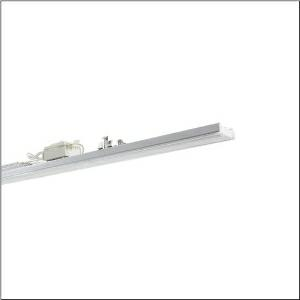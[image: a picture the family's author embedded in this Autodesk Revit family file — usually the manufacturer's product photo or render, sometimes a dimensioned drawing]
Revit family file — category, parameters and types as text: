
# Revit family: licross_11_recessed_mo_51te127n485g
name_source: partatom
category: Lighting Fixtures
units: mm (PartAtom-declared; Revit-internal decimal feet)

## family parameters
Cut with Voids When Loaded = No
Host = Face
Light Source = No
Part Type = Normal
Room Calculation Point = No
Round Connector Dimension = Use Diameter
Shared = No

## types (1)
- Licross 11 Recessed MO (1 x LED, 8950 lm, 48.5 W, 4000K)
    Apparent Load = 49 VA
    CIE Flux Codes = 67 92 99 100 100
    Color Rendering = 80
    Color Temperature = 4000K
    Default Elevation = 1800 mm
    Description = Licross 11 Recessed MO, luminaire insert, of sheet steel, galvanised, coil coated, white, length: 1.500mm, width: 66mm, height: 67mm, LED rated luminous flux: 8.950lm, light colour: 840, SDCM (Standard Deviation of Colour Matching)MacAdam ≤ 2 SDCM (initial), control gear: ON/OFF, with plug, 3-pole, with phase selection, mains connection: 220..240V, AC, 50/60Hz, rated input power: 49W, internal wiring halogen-free, primary optical cover: cover, of PMMA, light emission: direct distribution, primary light characteristic: symmetric, protection rating (complete): IP54, insulation class (complete): insulation class I (protective earthing), certification: CE, ENEC, VDE, UKCA, protection symbol: D if used in an environment with non-conductive dust loads with corresponding accessories, impact resistance: IK06, permissible ambient temperature for indoor applications: -35..+35°C, corresponds to IFS (International Featured Standards) requirements for safety and quality in the food industry, reducing of maximum allowable ambient temperature of 5°C with ceiling mounting, The light source and the operating device comply with the requirements of the Ecodesign Regulation (EU) 2019/2020 and are replaceable in accordance with this regulation, packaging unit: 1 piece
    Height = 58 mm
    Lamp = 1 x LED
    Lamp Light Flux = 8950 lm
    Lamp Power = 48.5 W
    Lamp count = 1
    Length = 1500 mm
    Luminous efficacy = 185 lm/W
    Manufacturer = Siteco
    ModVariant = No
    Model = 51TE127N485G
    Mounting Place = Ceiling
    Mounting Type = Pendant
    Number of Poles = 1
    OnlyDefault = Yes
    Power Factor = 1
    Product Name = Licross 11 Recessed MO
    Product group = luminaire insert | ceiling pendant
    ProductGroupID = 901
    Protection Class = Protection class I
    Protection Degree = IP 54
    RLX_Detail_Level = 1
    RLX_Emergency_Light_Flux = 0 lm
    RLX_Emergency_Type = 0
    RLX_Emergency_Type_DB = No
    RlxData = <blob elided: 21041 chars, md5=29e32cac>
    Socket = socket
    Standby Power = 0 W
    System Light Flux = 8950 lm
    System Power = 49 W
    Type Comments = Product without accessories
    Type Image = l_1296930.jpg
    URL = http://relux.com
    VarID = ---
    Voltage = 0 V
    Weight = 0.00 kg
    Width = 66 mm

## geometry (parser evidence)
native form markers: Blend x4, Sweep x11
no freeform markers — native parametric forms only
